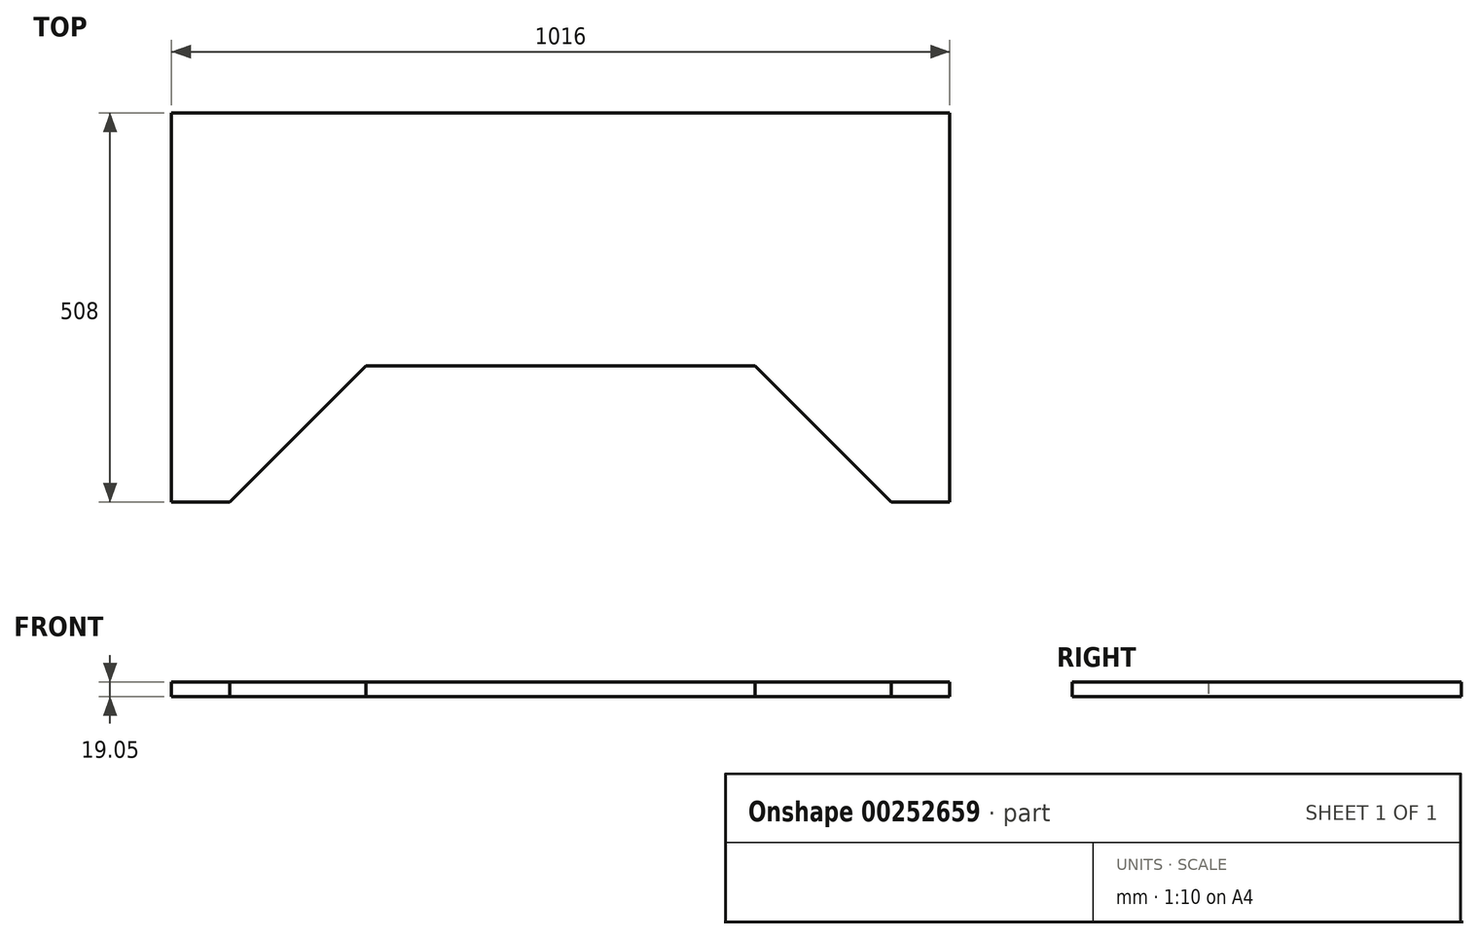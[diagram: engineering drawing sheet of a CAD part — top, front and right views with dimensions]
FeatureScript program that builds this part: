
annotation { "Feature Type Name" : "Feature", "Feature Type Description" : "" }
export const myFeature = defineFeature(function(context is Context, id is Id, definition is map)
    precondition{}
    {
        {
            var Q0;
            Q0=qCreatedBy(makeId("Top.planeOp"),FACE);
            var sketch = newSketch(context, id + "F0", { "sketchPlane" : qUnion([Q0])});
            skLineSegment(sketch, "E0.bottom", {"start": v(0, 0) * mm, "end": v(1016, 0) * mm});
            skLineSegment(sketch, "E0.left", {"start": v(0, 0) * mm, "end": v(0, -508) * mm});
            skLineSegment(sketch, "E0.right", {"start": v(1016, 0) * mm, "end": v(1016, -508) * mm});
            skLineSegment(sketch, "E1", {"start": v(508, 0) * mm, "end": v(508, -330.2) * mm, "construction": true});
            skLineSegment(sketch, "E2", {"start": v(0, -330.2) * mm, "end": v(1016, -330.2) * mm, "construction": true});
            skLineSegment(sketch, "E3", {"start": v(508, -330.2) * mm, "end": v(762, -330.2) * mm});
            skLineSegment(sketch, "E4", {"start": v(508, -330.2) * mm, "end": v(254, -330.2) * mm});
            skPoint(sketch, "E5.orphan", {"position": v(508, -508) * mm});
            skLineSegment(sketch, "E6", {"start": v(0, -508) * mm, "end": v(76.2, -508) * mm});
            skLineSegment(sketch, "E7", {"start": v(1016, -508) * mm, "end": v(939.8, -508) * mm});
            skLineSegment(sketch, "E8", {"start": v(939.8, -508) * mm, "end": v(762, -330.2) * mm});
            skLineSegment(sketch, "E9", {"start": v(254, -330.2) * mm, "end": v(76.2, -508) * mm});
            skSolve(sketch);
        }
        {
            var Q0;
            Q0=makeQuery(id+"F0.imprint","IMPRINT",FACE,{"disambiguationData":[TD([[makeQuery(id+"F0.imprint","IMPRINT",EDGE,{"derivedFrom":sQuery(id+"F0.wireOp",EDGE,"E0.bottom")}),-1.0]])]});
            extrude(context, id + "F1", {"entities" : qUnion([Q0]), "depth" : 19.05 * mm});
        }
    });
